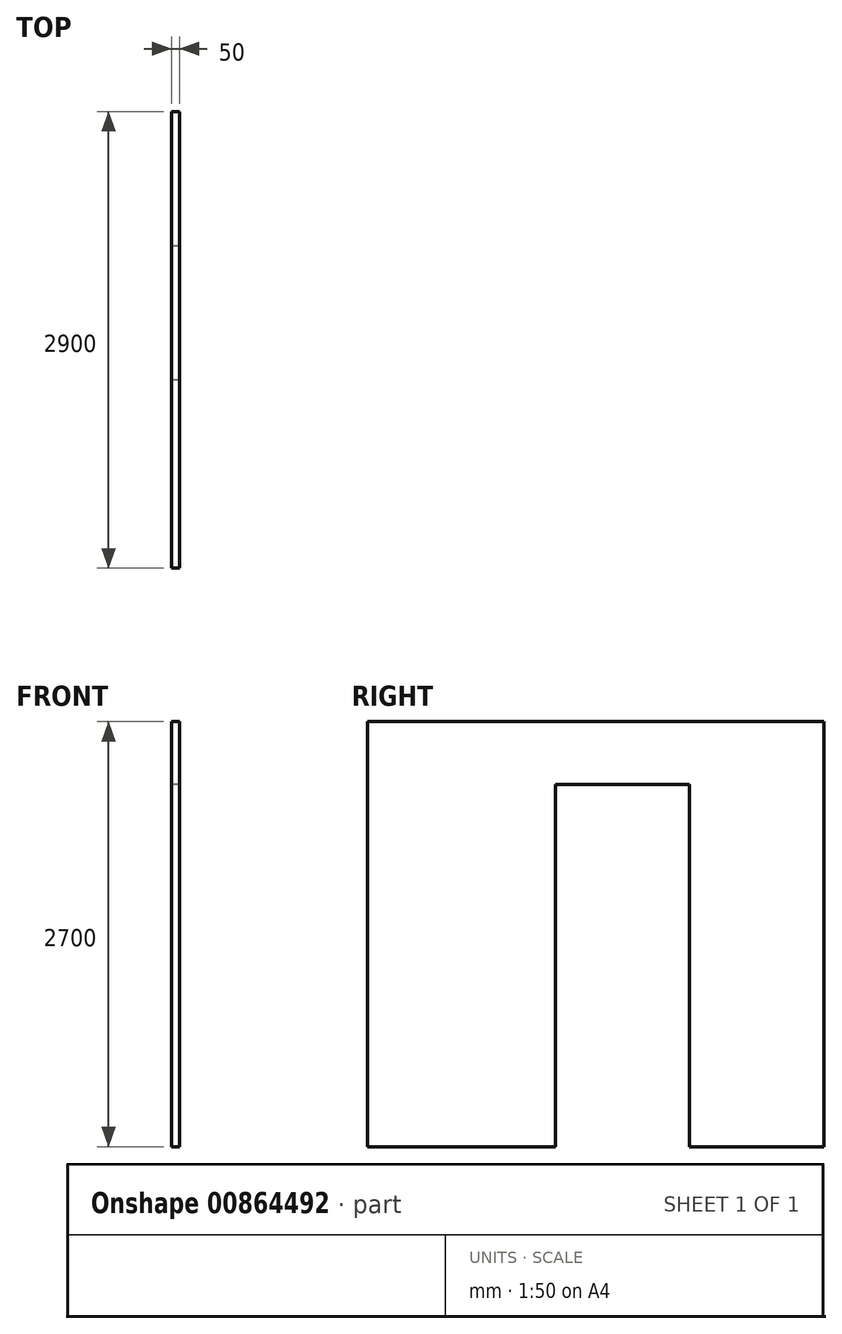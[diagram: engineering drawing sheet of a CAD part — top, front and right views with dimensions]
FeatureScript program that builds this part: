
annotation { "Feature Type Name" : "Feature", "Feature Type Description" : "" }
export const myFeature = defineFeature(function(context is Context, id is Id, definition is map)
    precondition{}
    {
        {
            var Q0;
            Q0=qCreatedBy(makeId("Right.planeOp"),FACE);
            var sketch = newSketch(context, id + "F0", { "sketchPlane" : qUnion([Q0])});
            skLineSegment(sketch, "E0.bottom", {"start": v(0, 0) * mm, "end": v(2900, 0) * mm});
            skLineSegment(sketch, "E0.top", {"start": v(0, 2700) * mm, "end": v(2900, 2700) * mm});
            skLineSegment(sketch, "E0.left", {"start": v(0, 0) * mm, "end": v(0, 2700) * mm});
            skLineSegment(sketch, "E0.right", {"start": v(2900, 0) * mm, "end": v(2900, 2700) * mm});
            skLineSegment(sketch, "E1.bottom", {"start": v(1194.75, 0) * mm, "end": v(2044.75, 0) * mm});
            skLineSegment(sketch, "E1.top", {"start": v(1194.75, 2300) * mm, "end": v(2044.75, 2300) * mm});
            skLineSegment(sketch, "E1.left", {"start": v(1194.75, 0) * mm, "end": v(1194.75, 2300) * mm});
            skLineSegment(sketch, "E1.right", {"start": v(2044.75, 0) * mm, "end": v(2044.75, 2300) * mm});
            skSolve(sketch);
        }
        {
            var Q0;
            Q0=makeQuery(id+"F0.imprint","IMPRINT",FACE,{"disambiguationData":[TD([[makeQuery(id+"F0.imprint","IMPRINT",EDGE,{"derivedFrom":sQuery(id+"F0.wireOp",EDGE,"E0.top")}),-1.0]])]});
            extrude(context, id + "F1", {"entities" : qUnion([Q0]), "depth" : 50 * mm, "offsetDistance" : 25 * mm});
        }
    });
